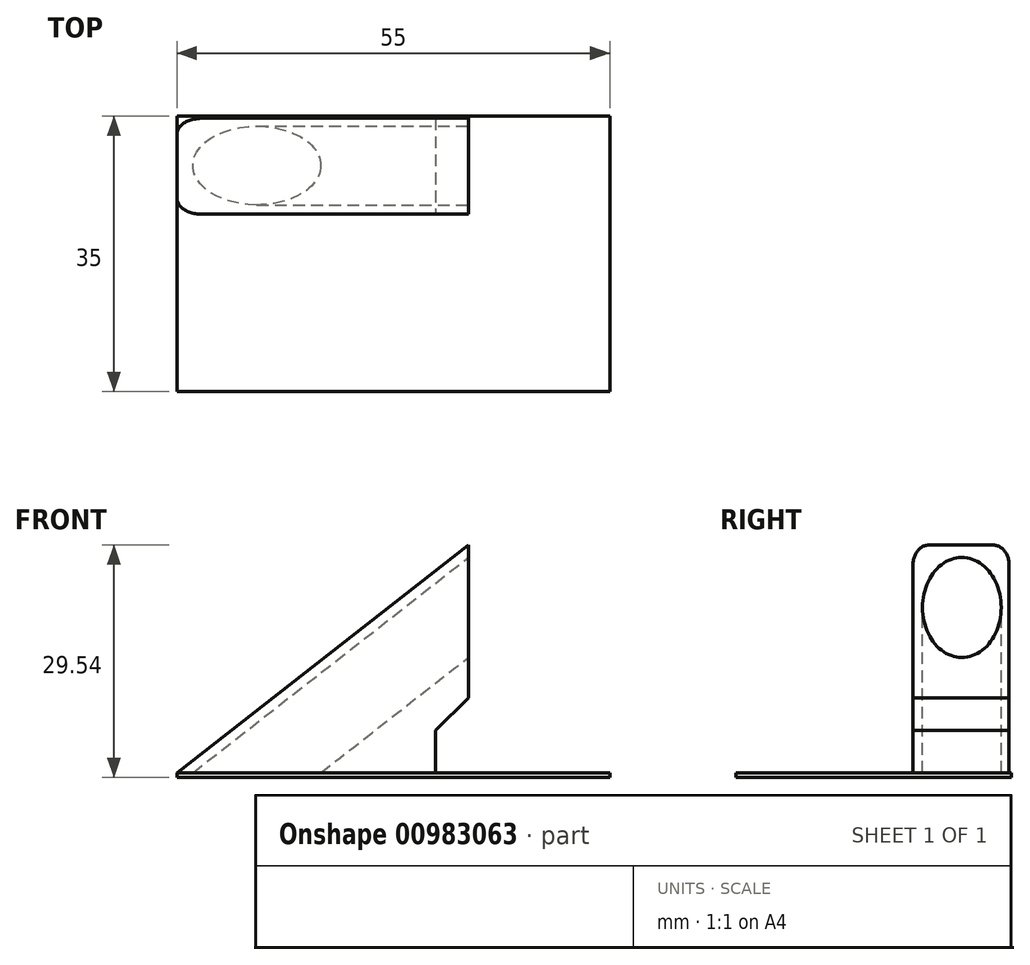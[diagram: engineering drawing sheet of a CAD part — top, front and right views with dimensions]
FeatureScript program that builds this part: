
annotation { "Feature Type Name" : "Feature", "Feature Type Description" : "" }
export const myFeature = defineFeature(function(context is Context, id is Id, definition is map)
    precondition{}
    {
        {
            var Q0;
            Q0=qCreatedBy(makeId("Top.planeOp"),FACE);
            var sketch = newSketch(context, id + "F0", { "sketchPlane" : qUnion([Q0])});
            skLineSegment(sketch, "E0.bottom", {"start": v(-27.5, 12.5) * mm, "end": v(27.5, 12.5) * mm});
            skLineSegment(sketch, "E0.top", {"start": v(-27.5, -22.5) * mm, "end": v(27.5, -22.5) * mm});
            skLineSegment(sketch, "E0.left", {"start": v(-27.5, 12.5) * mm, "end": v(-27.5, -22.5) * mm});
            skLineSegment(sketch, "E0.right", {"start": v(27.5, 12.5) * mm, "end": v(27.5, -22.5) * mm});
            skPoint(sketch, "E1", {"position": v(0, 12.5) * mm});
            skSolve(sketch);
        }
        {
            var Q0;
            Q0 = qSketchRegion(id + "F0", true);
            extrude(context, id + "F1", {"entities" : qUnion([Q0]), "depth" : .6 * mm, "offsetDistance" : 25 * mm});
        }
        {
            var Q0;
            Q0=qCreatedBy(makeId("Front.planeOp"),FACE);
            var sketch = newSketch(context, id + "F2", { "sketchPlane" : qUnion([Q0])});
            skPoint(sketch, "E2.0", {"position": v(-27.5, 0.6) * mm});
            skPoint(sketch, "E3.0", {"position": v(27.5, 0.6) * mm});
            skLineSegment(sketch, "E4", {"start": v(-27.5, 0.6) * mm, "end": v(9.54, 29.54) * mm});
            skLineSegment(sketch, "E5", {"start": v(-27.5, 0.6) * mm, "end": v(27.5, 0.6) * mm});
            skLineSegment(sketch, "E6", {"start": v(-17.35, 0.6) * mm, "end": v(37.65, 43.57) * mm, "construction": true});
            skLineSegment(sketch, "E7", {"start": v(-25.88, 0.6) * mm, "end": v(9.54, 28.27) * mm, "construction": true});
            skLineSegment(sketch, "E8", {"start": v(-8.82, 0.6) * mm, "end": v(39.96, 38.71) * mm, "construction": true});
            skLineSegment(sketch, "E9", {"start": v(0.68, 21.35) * mm, "end": v(7.15, 13.07) * mm, "construction": true});
            skPoint(sketch, "E10", {"position": v(3.91, 17.21) * mm});
            skLineSegment(sketch, "E11", {"start": v(9.54, 29.54) * mm, "end": v(9.54, 10.14) * mm});
            skLineSegment(sketch, "E12", {"start": v(5.37, 5.98) * mm, "end": v(5.37, 0.6) * mm});
            skLineSegment(sketch, "E13.trimOffspring", {"start": v(5.37, 5.98) * mm, "end": v(9.54, 10.14) * mm});
            skPoint(sketch, "E14.start.orphan", {"position": v(0, -2.84) * mm});
            skSolve(sketch);
        }
        {
            var Q0;
            Q0 = qSketchRegion(id + "F2", true);
            var Q1;
            Q1=makeQuery(id+"F1.opExtrude","SWEPT_FACE",FACE,{"disambiguationData":[OSD([sQuery(id+"F0.wireOp",EDGE,"E0.bottom")])]});
            extrude(context, id + "F3", {"entities" : qUnion([Q0]), "oppositeDirection" : true, "depth" : 12.2 * mm, "endBoundEntityFace" : qUnion([Q1]), "offsetDistance" : 25 * mm});
        }
        {
            var Q0;
            Q0=sQuery(id+"F2.wireOp",EDGE,"E9");
            cPlane(context, id + "F4", {"entities" : qUnion([Q0]), "cplaneType" : CPlaneType.LINE_ANGLE, "offset" : 25 * mm, "angle" : 0 * degree, "width" : 150 * mm, "height" : 150 * mm});
        }
        {
            var Q0;
            Q0=qCreatedBy(id+"F4.planeOp",FACE);
            var sketch = newSketch(context, id + "F5", { "sketchPlane" : qUnion([Q0])});
            skPoint(sketch, "E15.0", {"position": v(0, 11.15) * mm});
            skCircle(sketch, "E16", {"center": v(0, 11.15) * mm, "radius": 5 * mm});
            skSolve(sketch);
        }
        {
            var Q0;
            Q0 = qSketchRegion(id + "F5", true);
            var Q1;
            Q1 = qConstructionFilter(qBodyType(qCreatedBy(id + "F5" ,EDGE), BodyType.WIRE), ConstructionObject.NO);
            extrude(context, id + "F6", {"entities" : qUnion([Q0]), "surfaceOperationType" : NewSurfaceOperationType.ADD, "surfaceEntities" : qUnion([Q1]), "endBound" : BoundingType.SYMMETRIC, "depth" : 160 * mm, "offsetDistance" : 25 * mm});
        }
        {
            var Q0;
            Q0=makeQuery(id+"F6.opExtrude","SWEPT_BODY",BODY,{"disambiguationData":[OSD([sQuery(id+"F5.wireOp",EDGE,"E16")])]});
            var Q1;
            Q1=makeQuery(id+"F3.opExtrude","SWEPT_EDGE",EDGE,{"disambiguationData":[OSD([sQuery(id+"F2.wireOp",EDGE,"E4"),sQuery(id+"F2.wireOp",EDGE,"E11")])]});
            transform(context, id + "F7", {"entities" : qUnion([Q0]), "transformType" : TransformType.TRANSLATION_3D, "dx" : 0 * mm, "dy" : 6.2 * mm, "dz" : 0 * mm, "makeCopy" : false});
        }
        {
            var Q0;
            Q0=makeQuery(id+"F6.opExtrude","SWEPT_BODY",BODY,{"disambiguationData":[OSD([sQuery(id+"F5.wireOp",EDGE,"E16")])]});
            var Q1;
            Q1=makeQuery(id+"F3.opExtrude","SWEPT_BODY",BODY,{"disambiguationData":[OSD([sQuery(id+"F2.wireOp",EDGE,"E4"),sQuery(id+"F2.wireOp",EDGE,"E5"),sQuery(id+"F2.wireOp",EDGE,"E11"),sQuery(id+"F2.wireOp",EDGE,"mULyYKeY-y9qz-yML2-eM4z-TNHwhufcAOfd"),sQuery(id+"F2.wireOp",EDGE,"XJSorDhd-TECf-ZHiX-qBpx-E8FxiygHbOSN"),sQuery(id+"F2.wireOp",EDGE,"h5eVjUJy-EYBT-uWr2-vfxl-1hMbW3dewguE"),sQuery(id+"F2.wireOp",EDGE,"efcb19b8-5d4d-4313-9923-d2eb0aca2e07.trimOffspring")])]});
            booleanBodies(context, id + "F8", {"operationType" : BooleanOperationType.SUBTRACTION, "tools" : qUnion([Q0]), "targets" : qUnion([Q1])});
        }
        {
            var Q0;
            Q0=makeQuery(id+"F3.opExtrude","CAP_EDGE",EDGE,{"disambiguationData":[OSD([sQuery(id+"F2.wireOp",EDGE,"E4")])],"isStart":false});
            var Q1;
            Q1=makeQuery(id+"F3.opExtrude","CAP_EDGE",EDGE,{"disambiguationData":[OSD([sQuery(id+"F2.wireOp",EDGE,"E4")])],"isStart":true});
            fillet(context, id + "F9", {"entities" : qUnion([Q0, Q1]), "radius" : 2 * mm, "tangentPropagation" : true, "allowEdgeOverflow" : false});
        }
    });
